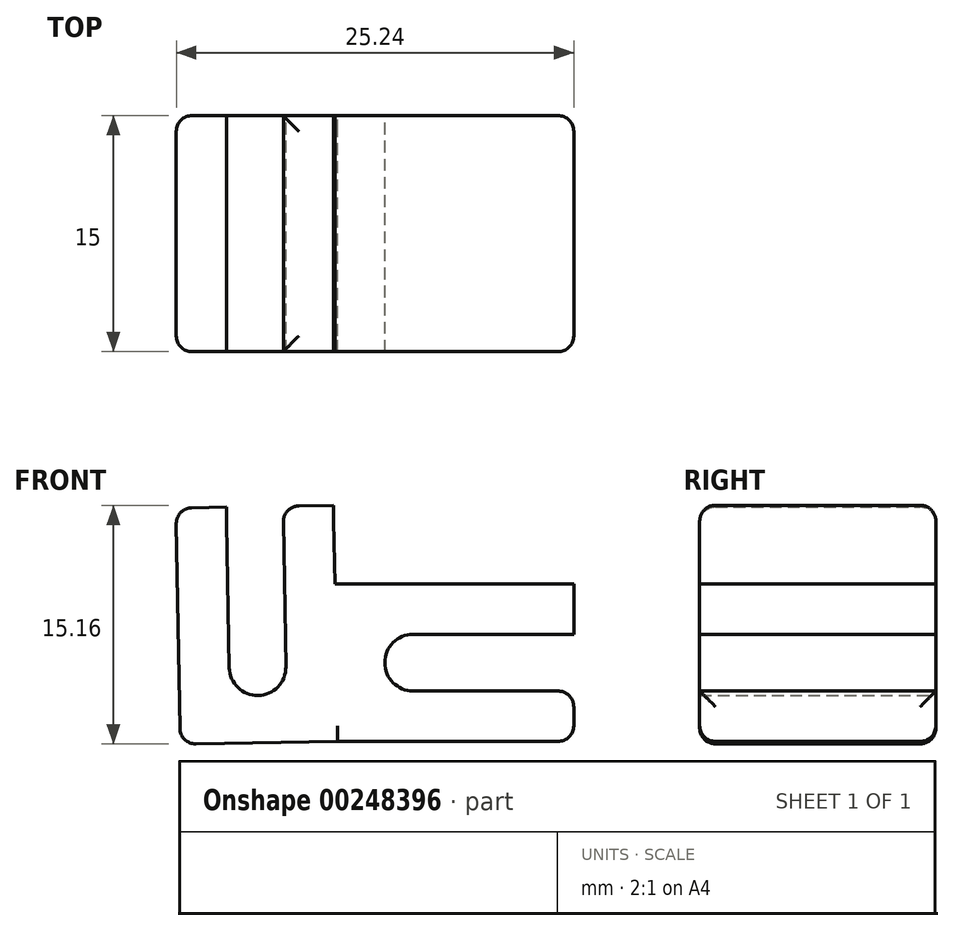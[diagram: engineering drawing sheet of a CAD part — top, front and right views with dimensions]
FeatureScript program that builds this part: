
annotation { "Feature Type Name" : "Feature", "Feature Type Description" : "" }
export const myFeature = defineFeature(function(context is Context, id is Id, definition is map)
    precondition{}
    {
        {
            var Q0;
            Q0=qCreatedBy(makeId("Top.planeOp"),FACE);
            var sketch = newSketch(context, id + "F0", { "sketchPlane" : qUnion([Q0])});
            skLineSegment(sketch, "E0.bottom", {"start": v(0, 0) * mm, "end": v(15, 0) * mm});
            skLineSegment(sketch, "E0.top", {"start": v(0, 15) * mm, "end": v(15, 15) * mm});
            skLineSegment(sketch, "E0.left", {"start": v(0, 0) * mm, "end": v(0, 15) * mm});
            skLineSegment(sketch, "E0.right", {"start": v(15, 0) * mm, "end": v(15, 15) * mm});
            skSolve(sketch);
        }
        {
            var Q0;
            Q0=makeQuery(id+"F0.imprint","IMPRINT",FACE,{"disambiguationData":[TD([[makeQuery(id+"F0.imprint","IMPRINT",EDGE,{"derivedFrom":sQuery(id+"F0.wireOp",EDGE,"E0.bottom")}),1.0]])]});
            extrude(context, id + "F1", {"entities" : qUnion([Q0]), "depth" : 10 * mm});
        }
        {
            var Q0;
            Q0=makeQuery(id+"F1.opExtrude","SWEPT_FACE",FACE,{"disambiguationData":[OSD([sQuery(id+"F0.wireOp",EDGE,"E0.right")])]});
            var sketch = newSketch(context, id + "F2", { "sketchPlane" : qUnion([Q0])});
            skLineSegment(sketch, "E1.bottom", {"start": v(0, 6.8) * mm, "end": v(15, 6.8) * mm});
            skLineSegment(sketch, "E1.top", {"start": v(0, 3.2) * mm, "end": v(15, 3.2) * mm});
            skLineSegment(sketch, "E1.left", {"start": v(0, 6.8) * mm, "end": v(0, 3.2) * mm});
            skLineSegment(sketch, "E1.right", {"start": v(15, 6.8) * mm, "end": v(15, 3.2) * mm});
            skSolve(sketch);
        }
        {
            var Q0;
            Q0=qSketchRegion(id+"F2",true);
            extrude(context, id + "F3", {"entities" : qUnion([Q0]), "operationType" : NewBodyOperationType.REMOVE, "oppositeDirection" : true, "depth" : 12 * mm});
        }
        {
            var Q0;
            Q0=makeQuery(id+"F3.boolean.opBoolean","COPY",EDGE,{"derivedFrom":makeQuery(id+"F3.opExtrude","CAP_EDGE",EDGE,{"disambiguationData":[OSD([sQuery(id+"F2.wireOp",EDGE,"E1.top")])],"isStart":false})});
            var Q1;
            Q1=makeQuery(id+"F3.boolean.opBoolean","COPY",EDGE,{"derivedFrom":makeQuery(id+"F3.opExtrude","CAP_EDGE",EDGE,{"disambiguationData":[OSD([sQuery(id+"F2.wireOp",EDGE,"E1.bottom")])],"isStart":false})});
            fillet(context, id + "F4", {"entities" : qUnion([Q0, Q1]), "radius" : 1.8 * mm, "tangentPropagation" : true, "allowEdgeOverflow" : false});
        }
        {
            var Q0;
            Q0=makeQuery(id+"F1.opExtrude","SWEPT_BODY",BODY,{"disambiguationData":[OSD([sQuery(id+"F0.wireOp",EDGE,"E0.bottom"),sQuery(id+"F0.wireOp",EDGE,"E0.top"),sQuery(id+"F0.wireOp",EDGE,"E0.left"),sQuery(id+"F0.wireOp",EDGE,"E0.right")])]});
            var Q1;
            Q1=makeQuery(id+"F1.opExtrude","CAP_EDGE",EDGE,{"disambiguationData":[OSD([sQuery(id+"F0.wireOp",EDGE,"E0.left")])],"isStart":true});
            circularPattern(context, id + "F5", {"entities" : qUnion([Q0]), "axis" : qUnion([Q1]), "angle" : 91 * degree, "instanceCount" : 2, "oppositeDirection" : true, "equalSpace" : true});
        }
        {
            var Q0;
            Q0=makeQuery(id+"F1.opExtrude","SWEPT_FACE",FACE,{"disambiguationData":[OSD([sQuery(id+"F0.wireOp",EDGE,"E0.bottom")])]});
            var sketch = newSketch(context, id + "F6", { "sketchPlane" : qUnion([Q0])});
            skLineSegment(sketch, "E2", {"start": v(0, 10) * mm, "end": v(-0.17, 10) * mm});
            skLineSegment(sketch, "E3", {"start": v(-0.17, 10) * mm, "end": v(0, 0) * mm});
            skLineSegment(sketch, "E4", {"start": v(0, 0) * mm, "end": v(0, 10) * mm});
            skSolve(sketch);
        }
        {
            var Q0;
            Q0=qSketchRegion(id+"F6",true);
            var Q1;
            Q1=makeQuery(id+"F1.opExtrude","SWEPT_FACE",FACE,{"disambiguationData":[OSD([sQuery(id+"F0.wireOp",EDGE,"E0.top")])]});
            extrude(context, id + "F7", {"entities" : qUnion([Q0]), "operationType" : NewBodyOperationType.ADD, "endBound" : BoundingType.UP_TO_SURFACE, "oppositeDirection" : true, "endBoundEntityFace" : qUnion([Q1]), "depth" : 25 * mm});
        }
        {
            var Q0;
            Q0=makeQuery(id+"F3.boolean.opBoolean","COPY",EDGE,{"derivedFrom":makeQuery(id+"F3.opExtrude","SWEPT_EDGE",EDGE,{"disambiguationData":[OSD([sQuery(id+"F0.wireOp",EDGE,"E0.bottom"),sQuery(id+"F0.wireOp",EDGE,"E0.right"),sQuery(id+"F2.wireOp",EDGE,"E1.bottom"),sQuery(id+"F2.wireOp",EDGE,"E1.left")])]})});
            var Q1;
            Q1=makeQuery(id+"F3.boolean.opBoolean","COPY",EDGE,{"derivedFrom":makeQuery(id+"F3.opExtrude","CAP_EDGE",EDGE,{"disambiguationData":[OSD([sQuery(id+"F2.wireOp",EDGE,"E1.bottom")])],"isStart":true})});
            var Q2;
            {var subQ0=sQuery(id+"F0.wireOp",EDGE,"E0.right");var subQ1=sQuery(id+"F0.wireOp",EDGE,"E0.top");Q2=makeQuery(id+"F3.boolean.opBoolean","SPLIT",EDGE,{"disambiguationData":[TD([makeQuery(id+"F3.opExtrude","SWEPT_FACE",FACE,{"disambiguationData":[OSD([sQuery(id+"F2.wireOp",EDGE,"E1.top")])]})])],"derivedFrom":makeQuery(id+"F1.opExtrude","SWEPT_EDGE",EDGE,{"disambiguationData":[OSD([subQ1,subQ0])]})});}
            var Q3;
            {var subQ0=sQuery(id+"F0.wireOp",EDGE,"E0.bottom");var subQ1=sQuery(id+"F0.wireOp",EDGE,"E0.right");Q3=makeQuery(id+"F3.boolean.opBoolean","SPLIT",EDGE,{"disambiguationData":[TD([makeQuery(id+"F3.opExtrude","SWEPT_FACE",FACE,{"disambiguationData":[OSD([sQuery(id+"F2.wireOp",EDGE,"E1.top")])]})])],"derivedFrom":makeQuery(id+"F1.opExtrude","SWEPT_EDGE",EDGE,{"disambiguationData":[OSD([subQ0,subQ1])]})});}
            var Q4;
            Q4=makeQuery(id+"F3.boolean.opBoolean","COPY",EDGE,{"derivedFrom":makeQuery(id+"F3.opExtrude","CAP_EDGE",EDGE,{"disambiguationData":[OSD([sQuery(id+"F2.wireOp",EDGE,"E1.top")])],"isStart":true})});
            var Q5;
            Q5=makeQuery(id+"F3.boolean.opBoolean","COPY",EDGE,{"derivedFrom":makeQuery(id+"F3.opExtrude","SWEPT_EDGE",EDGE,{"disambiguationData":[OSD([sQuery(id+"F0.wireOp",EDGE,"E0.top"),sQuery(id+"F0.wireOp",EDGE,"E0.right"),sQuery(id+"F2.wireOp",EDGE,"E1.top"),sQuery(id+"F2.wireOp",EDGE,"E1.right")])]})});
            var Q6;
            Q6=makeQuery(id+"F1.opExtrude","CAP_EDGE",EDGE,{"disambiguationData":[OSD([sQuery(id+"F0.wireOp",EDGE,"E0.right")])],"isStart":true});
            var Q7;
            Q7=makeQuery(id+"F5.opPattern","COPY",EDGE,{"derivedFrom":makeQuery(id+"F1.opExtrude","CAP_EDGE",EDGE,{"disambiguationData":[OSD([sQuery(id+"F0.wireOp",EDGE,"E0.bottom")])],"isStart":false}),"instanceName":"1"});
            var Q8;
            Q8=makeQuery(id+"F5.opPattern","COPY",EDGE,{"derivedFrom":makeQuery(id+"F3.boolean.opBoolean","COPY",EDGE,{"derivedFrom":makeQuery(id+"F3.opExtrude","SWEPT_EDGE",EDGE,{"disambiguationData":[OSD([sQuery(id+"F0.wireOp",EDGE,"E0.bottom"),sQuery(id+"F0.wireOp",EDGE,"E0.right"),sQuery(id+"F2.wireOp",EDGE,"E1.bottom"),sQuery(id+"F2.wireOp",EDGE,"E1.left")])]})}),"instanceName":"1"});
            var Q9;
            {var subQ0=sQuery(id+"F0.wireOp",EDGE,"E0.bottom");var subQ1=sQuery(id+"F0.wireOp",EDGE,"E0.right");Q9=makeQuery(id+"F5.opPattern","COPY",EDGE,{"derivedFrom":makeQuery(id+"F3.boolean.opBoolean","SPLIT",EDGE,{"disambiguationData":[TD([makeQuery(id+"F3.opExtrude","SWEPT_FACE",FACE,{"disambiguationData":[OSD([sQuery(id+"F2.wireOp",EDGE,"E1.bottom")])]})])],"derivedFrom":makeQuery(id+"F1.opExtrude","SWEPT_EDGE",EDGE,{"disambiguationData":[OSD([subQ0,subQ1])]})}),"instanceName":"1"});}
            var Q10;
            Q10=makeQuery(id+"F5.opPattern","COPY",EDGE,{"derivedFrom":makeQuery(id+"F3.boolean.opBoolean","COPY",EDGE,{"derivedFrom":makeQuery(id+"F3.opExtrude","CAP_EDGE",EDGE,{"disambiguationData":[OSD([sQuery(id+"F2.wireOp",EDGE,"E1.bottom")])],"isStart":true})}),"instanceName":"1"});
            var Q11;
            {var subQ0=sQuery(id+"F0.wireOp",EDGE,"E0.right");var subQ1=sQuery(id+"F0.wireOp",EDGE,"E0.top");Q11=makeQuery(id+"F5.opPattern","COPY",EDGE,{"derivedFrom":makeQuery(id+"F3.boolean.opBoolean","SPLIT",EDGE,{"disambiguationData":[TD([makeQuery(id+"F3.opExtrude","SWEPT_FACE",FACE,{"disambiguationData":[OSD([sQuery(id+"F2.wireOp",EDGE,"E1.bottom")])]})])],"derivedFrom":makeQuery(id+"F1.opExtrude","SWEPT_EDGE",EDGE,{"disambiguationData":[OSD([subQ1,subQ0])]})}),"instanceName":"1"});}
            var Q12;
            Q12=makeQuery(id+"F5.opPattern","COPY",EDGE,{"derivedFrom":makeQuery(id+"F1.opExtrude","CAP_EDGE",EDGE,{"disambiguationData":[OSD([sQuery(id+"F0.wireOp",EDGE,"E0.right")])],"isStart":false}),"instanceName":"1"});
            var Q13;
            Q13=makeQuery(id+"F5.opPattern","COPY",EDGE,{"derivedFrom":makeQuery(id+"F1.opExtrude","CAP_EDGE",EDGE,{"disambiguationData":[OSD([sQuery(id+"F0.wireOp",EDGE,"E0.left")])],"isStart":false}),"instanceName":"1"});
            var Q14;
            Q14=makeQuery(id+"F5.opPattern","COPY",EDGE,{"derivedFrom":makeQuery(id+"F1.opExtrude","CAP_EDGE",EDGE,{"disambiguationData":[OSD([sQuery(id+"F0.wireOp",EDGE,"E0.top")])],"isStart":false}),"instanceName":"1"});
            var Q15;
            Q15=makeQuery(id+"F5.opPattern","COPY",EDGE,{"derivedFrom":makeQuery(id+"F3.boolean.opBoolean","COPY",EDGE,{"derivedFrom":makeQuery(id+"F3.opExtrude","CAP_EDGE",EDGE,{"disambiguationData":[OSD([sQuery(id+"F2.wireOp",EDGE,"E1.top")])],"isStart":true})}),"instanceName":"1"});
            var Q16;
            Q16=makeQuery(id+"F5.opPattern","COPY",EDGE,{"derivedFrom":makeQuery(id+"F1.opExtrude","SWEPT_EDGE",EDGE,{"disambiguationData":[OSD([sQuery(id+"F0.wireOp",EDGE,"E0.bottom"),sQuery(id+"F0.wireOp",EDGE,"E0.left")])]}),"instanceName":"1"});
            var Q17;
            Q17=makeQuery(id+"F1.opExtrude","CAP_EDGE",EDGE,{"disambiguationData":[OSD([sQuery(id+"F0.wireOp",EDGE,"E0.bottom")])],"isStart":true});
            var Q18;
            Q18=makeQuery(id+"F1.opExtrude","CAP_EDGE",EDGE,{"disambiguationData":[OSD([sQuery(id+"F0.wireOp",EDGE,"E0.top")])],"isStart":true});
            var Q19;
            Q19=makeQuery(id+"F5.opPattern","COPY",EDGE,{"derivedFrom":makeQuery(id+"F1.opExtrude","SWEPT_EDGE",EDGE,{"disambiguationData":[OSD([sQuery(id+"F0.wireOp",EDGE,"E0.top"),sQuery(id+"F0.wireOp",EDGE,"E0.left")])]}),"instanceName":"1"});
            var Q20;
            {var subQ0=sQuery(id+"F0.wireOp",EDGE,"E0.bottom");var subQ1=sQuery(id+"F0.wireOp",EDGE,"E0.right");Q20=makeQuery(id+"F3.boolean.opBoolean","SPLIT",EDGE,{"disambiguationData":[TD([makeQuery(id+"F3.opExtrude","SWEPT_FACE",FACE,{"disambiguationData":[OSD([sQuery(id+"F2.wireOp",EDGE,"E1.bottom")])]})])],"derivedFrom":makeQuery(id+"F1.opExtrude","SWEPT_EDGE",EDGE,{"disambiguationData":[OSD([subQ0,subQ1])]})});}
            var Q21;
            {var subQ0=sQuery(id+"F0.wireOp",EDGE,"E0.right");var subQ1=sQuery(id+"F0.wireOp",EDGE,"E0.top");Q21=makeQuery(id+"F3.boolean.opBoolean","SPLIT",EDGE,{"disambiguationData":[TD([makeQuery(id+"F3.opExtrude","SWEPT_FACE",FACE,{"disambiguationData":[OSD([sQuery(id+"F2.wireOp",EDGE,"E1.bottom")])]})])],"derivedFrom":makeQuery(id+"F1.opExtrude","SWEPT_EDGE",EDGE,{"disambiguationData":[OSD([subQ1,subQ0])]})});}
            var Q22;
            {var subQ0=sQuery(id+"F0.wireOp",EDGE,"E0.bottom");var subQ1=sQuery(id+"F0.wireOp",EDGE,"E0.right");Q22=makeQuery(id+"F5.opPattern","COPY",EDGE,{"derivedFrom":makeQuery(id+"F3.boolean.opBoolean","SPLIT",EDGE,{"disambiguationData":[TD([makeQuery(id+"F3.opExtrude","SWEPT_FACE",FACE,{"disambiguationData":[OSD([sQuery(id+"F2.wireOp",EDGE,"E1.top")])]})])],"derivedFrom":makeQuery(id+"F1.opExtrude","SWEPT_EDGE",EDGE,{"disambiguationData":[OSD([subQ0,subQ1])]})}),"instanceName":"1"});}
            var Q23;
            Q23=makeQuery(id+"FjorjNvqaMhOX3O_1.opExtrude","CAP_EDGE",EDGE,{"disambiguationData":[OSD([sQuery(id+"F5jBgX5IeeNHT91_1.wireOp",EDGE,"wImvANcf-EoSg-NlkI-oFaj-ks3O6YM71ejX")])],"isStart":true});
            var Q24;
            {var subQ0=sQuery(id+"F0.wireOp",EDGE,"E0.right");var subQ1=sQuery(id+"F0.wireOp",EDGE,"E0.top");Q24=makeQuery(id+"F5.opPattern","COPY",EDGE,{"derivedFrom":makeQuery(id+"F3.boolean.opBoolean","SPLIT",EDGE,{"disambiguationData":[TD([makeQuery(id+"F3.opExtrude","SWEPT_FACE",FACE,{"disambiguationData":[OSD([sQuery(id+"F2.wireOp",EDGE,"E1.top")])]})])],"derivedFrom":makeQuery(id+"F1.opExtrude","SWEPT_EDGE",EDGE,{"disambiguationData":[OSD([subQ1,subQ0])]})}),"instanceName":"1"});}
            var Q25;
            {var subQ0=sQuery(id+"F0.wireOp",EDGE,"E0.top");Q25=makeQuery(id+"FjorjNvqaMhOX3O_1.opExtrude","TWEAK_EDGE",EDGE,{"derivedFrom":[makeQuery(id+"F7.boolean.opBoolean","MERGE",FACE,{"derivedFrom":[makeQuery(id+"F1.opExtrude","SWEPT_FACE",FACE,{"disambiguationData":[OSD([subQ0])]}),makeQuery(id+"F7.opExtrude","CAP_FACE",FACE,{"disambiguationData":[OSD([subQ0])],"isStart":false})]}),makeQuery(id+"F5jBgX5IeeNHT91_1.imprint","IMPRINT",EDGE,{"derivedFrom":sQuery(id+"F5jBgX5IeeNHT91_1.wireOp",EDGE,"wImvANcf-EoSg-NlkI-oFaj-ks3O6YM71ejX")})]});}
            fillet(context, id + "F8", {"entities" : qUnion([Q0, Q1, Q2, Q3, Q4, Q5, Q6, Q7, Q8, Q9, Q10, Q11, Q12, Q13, Q14, Q15, Q16, Q17, Q18, Q19, Q20, Q21, Q22, Q23, Q24, Q25]), "radius" : 1 * mm, "tangentPropagation" : true, "allowEdgeOverflow" : false});
        }
    });
